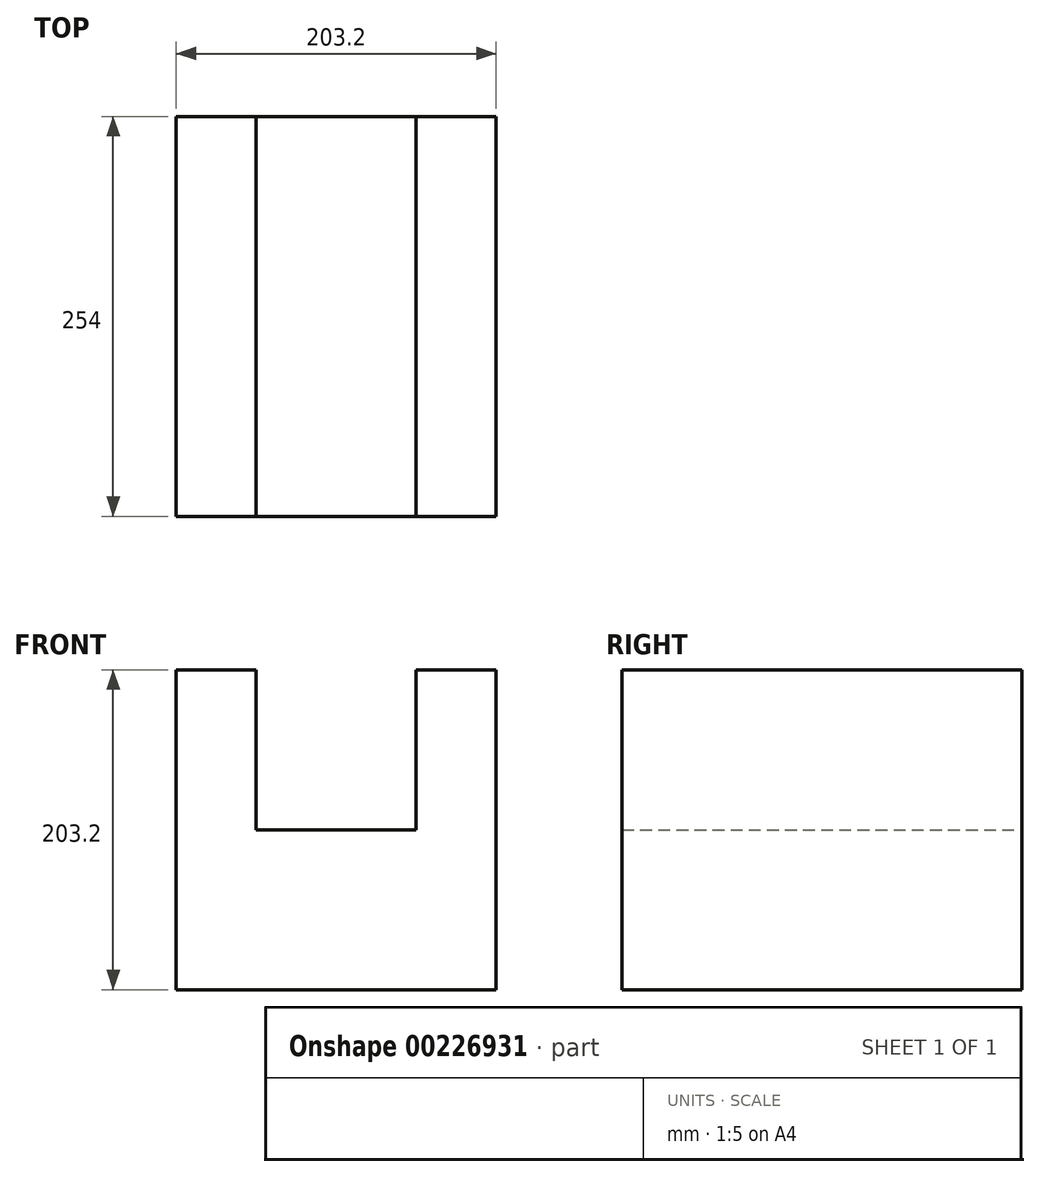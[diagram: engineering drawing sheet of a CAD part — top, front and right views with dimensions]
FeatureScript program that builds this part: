
annotation { "Feature Type Name" : "Feature", "Feature Type Description" : "" }
export const myFeature = defineFeature(function(context is Context, id is Id, definition is map)
    precondition{}
    {
        {
            var Q0;
            Q0=qCreatedBy(makeId("Front.planeOp"),FACE);
            var sketch = newSketch(context, id + "F0", { "sketchPlane" : qUnion([Q0])});
            skLineSegment(sketch, "E0.bottom", {"start": v(92.7, 116.85) * mm, "end": v(143.5, 116.85) * mm});
            skLineSegment(sketch, "E0.top", {"start": v(92.7, -86.35) * mm, "end": v(295.9, -86.35) * mm});
            skLineSegment(sketch, "E0.left", {"start": v(92.7, 116.85) * mm, "end": v(92.7, -86.35) * mm});
            skLineSegment(sketch, "E0.right", {"start": v(295.9, 116.85) * mm, "end": v(295.9, -86.35) * mm});
            skLineSegment(sketch, "E1", {"start": v(143.5, 116.85) * mm, "end": v(143.5, 15.25) * mm});
            skLineSegment(sketch, "E2", {"start": v(143.5, 15.25) * mm, "end": v(245.1, 15.25) * mm});
            skLineSegment(sketch, "E3", {"start": v(245.1, 15.25) * mm, "end": v(245.1, 116.85) * mm});
            skLineSegment(sketch, "E4.trimOffspring", {"start": v(245.1, 116.85) * mm, "end": v(295.9, 116.85) * mm});
            skLineSegment(sketch, "E5", {"start": v(143.5, 116.85) * mm, "end": v(92.7, 116.85) * mm});
            skLineSegment(sketch, "E6", {"start": v(245.1, 15.25) * mm, "end": v(143.5, 15.25) * mm});
            skLineSegment(sketch, "E7", {"start": v(295.9, -86.35) * mm, "end": v(295.9, 116.85) * mm});
            skLineSegment(sketch, "E8", {"start": v(295.9, -86.35) * mm, "end": v(92.7, -86.35) * mm});
            skLineSegment(sketch, "E9", {"start": v(92.7, -86.35) * mm, "end": v(92.7, 116.85) * mm});
            skLineSegment(sketch, "E10", {"start": v(143.5, 15.25) * mm, "end": v(143.5, 116.85) * mm});
            skSolve(sketch);
        }
        {
            var Q0;
            Q0=makeQuery(id+"F0.imprint","IMPRINT",FACE,{"disambiguationData":[TD([[makeQuery(id+"F0.imprint","IMPRINT",EDGE,{"derivedFrom":sQuery(id+"F0.wireOp",EDGE,"E4.trimOffspring")}),-1.0]])]});
            extrude(context, id + "F1", {"entities" : qUnion([Q0]), "depth" : 254 * mm});
        }
    });
